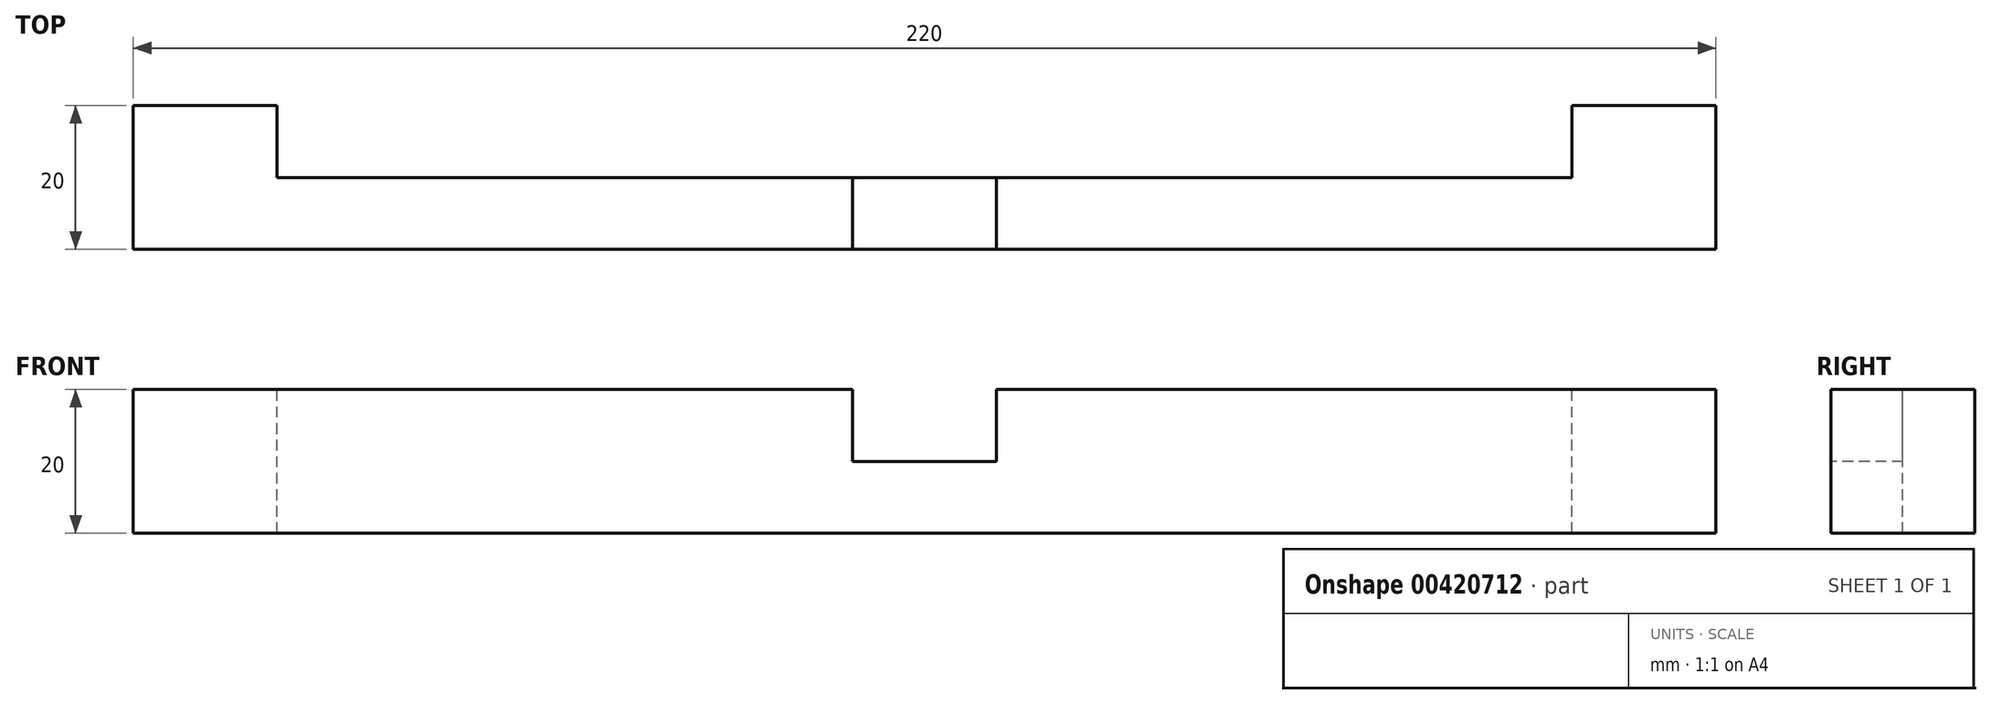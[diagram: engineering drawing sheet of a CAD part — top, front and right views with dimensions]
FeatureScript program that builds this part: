
annotation { "Feature Type Name" : "Feature", "Feature Type Description" : "" }
export const myFeature = defineFeature(function(context is Context, id is Id, definition is map)
    precondition{}
    {
        {
            var Q0;
            Q0=qCreatedBy(makeId("Right.planeOp"),FACE);
            var sketch = newSketch(context, id + "F0", { "sketchPlane" : qUnion([Q0])});
            skLineSegment(sketch, "E0.bottom", {"start": v(10, 10) * mm, "end": v(-10, 10) * mm});
            skLineSegment(sketch, "E0.top", {"start": v(10, -10) * mm, "end": v(-10, -10) * mm});
            skLineSegment(sketch, "E0.left", {"start": v(10, 10) * mm, "end": v(10, -10) * mm});
            skLineSegment(sketch, "E0.right", {"start": v(-10, 10) * mm, "end": v(-10, -10) * mm});
            skPoint(sketch, "E0.middle", {"position": v(0, 0) * mm});
            skSolve(sketch);
        }
        {
            var Q0;
            Q0=qSketchRegion(id+"F0",true);
            extrude(context, id + "F1", {"entities" : qUnion([Q0]), "endBound" : BoundingType.SYMMETRIC, "depth" : 220 * mm});
        }
        {
            var Q0;
            Q0=makeQuery(id+"F1.opExtrude","SWEPT_FACE",FACE,{"disambiguationData":[OSD([sQuery(id+"F0.wireOp",EDGE,"E0.right")])]});
            var sketch = newSketch(context, id + "F2", { "sketchPlane" : qUnion([Q0])});
            skLineSegment(sketch, "E1.bottom", {"start": v(-10, 10) * mm, "end": v(10, 10) * mm});
            skLineSegment(sketch, "E1.top", {"start": v(-10, 0) * mm, "end": v(10, 0) * mm});
            skLineSegment(sketch, "E1.left", {"start": v(-10, 10) * mm, "end": v(-10, 0) * mm});
            skLineSegment(sketch, "E1.right", {"start": v(10, 10) * mm, "end": v(10, 0) * mm});
            skSolve(sketch);
        }
        {
            var Q0;
            Q0=qSketchRegion(id+"F2",true);
            extrude(context, id + "F3", {"entities" : qUnion([Q0]), "operationType" : NewBodyOperationType.REMOVE, "oppositeDirection" : true, "depth" : 20 * mm});
        }
        {
            var Q0;
            {var subQ2=sQuery(id+"F0.wireOp",EDGE,"E0.bottom");Q0=makeQuery(id+"F3.boolean.opBoolean","SPLIT",FACE,{"disambiguationData":[TD([makeQuery(id+"F3.opExtrude","SWEPT_FACE",FACE,{"disambiguationData":[OSD([sQuery(id+"F2.wireOp",EDGE,"E1.right")])]})])],"derivedFrom":makeQuery(id+"F1.opExtrude","SWEPT_FACE",FACE,{"disambiguationData":[OSD([subQ2])]})});}
            var sketch = newSketch(context, id + "F4", { "sketchPlane" : qUnion([Q0])});
            skLineSegment(sketch, "E2.bottom", {"start": v(-90, 10) * mm, "end": v(90, 10) * mm});
            skLineSegment(sketch, "E2.top", {"start": v(-90, 0) * mm, "end": v(90, 0) * mm});
            skLineSegment(sketch, "E2.left", {"start": v(-90, 10) * mm, "end": v(-90, 0) * mm});
            skLineSegment(sketch, "E2.right", {"start": v(90, 10) * mm, "end": v(90, 0) * mm});
            skSolve(sketch);
        }
        {
            var Q0;
            Q0=qSketchRegion(id+"F4",true);
            extrude(context, id + "F5", {"entities" : qUnion([Q0]), "operationType" : NewBodyOperationType.REMOVE, "oppositeDirection" : true, "depth" : 20 * mm});
        }
    });
